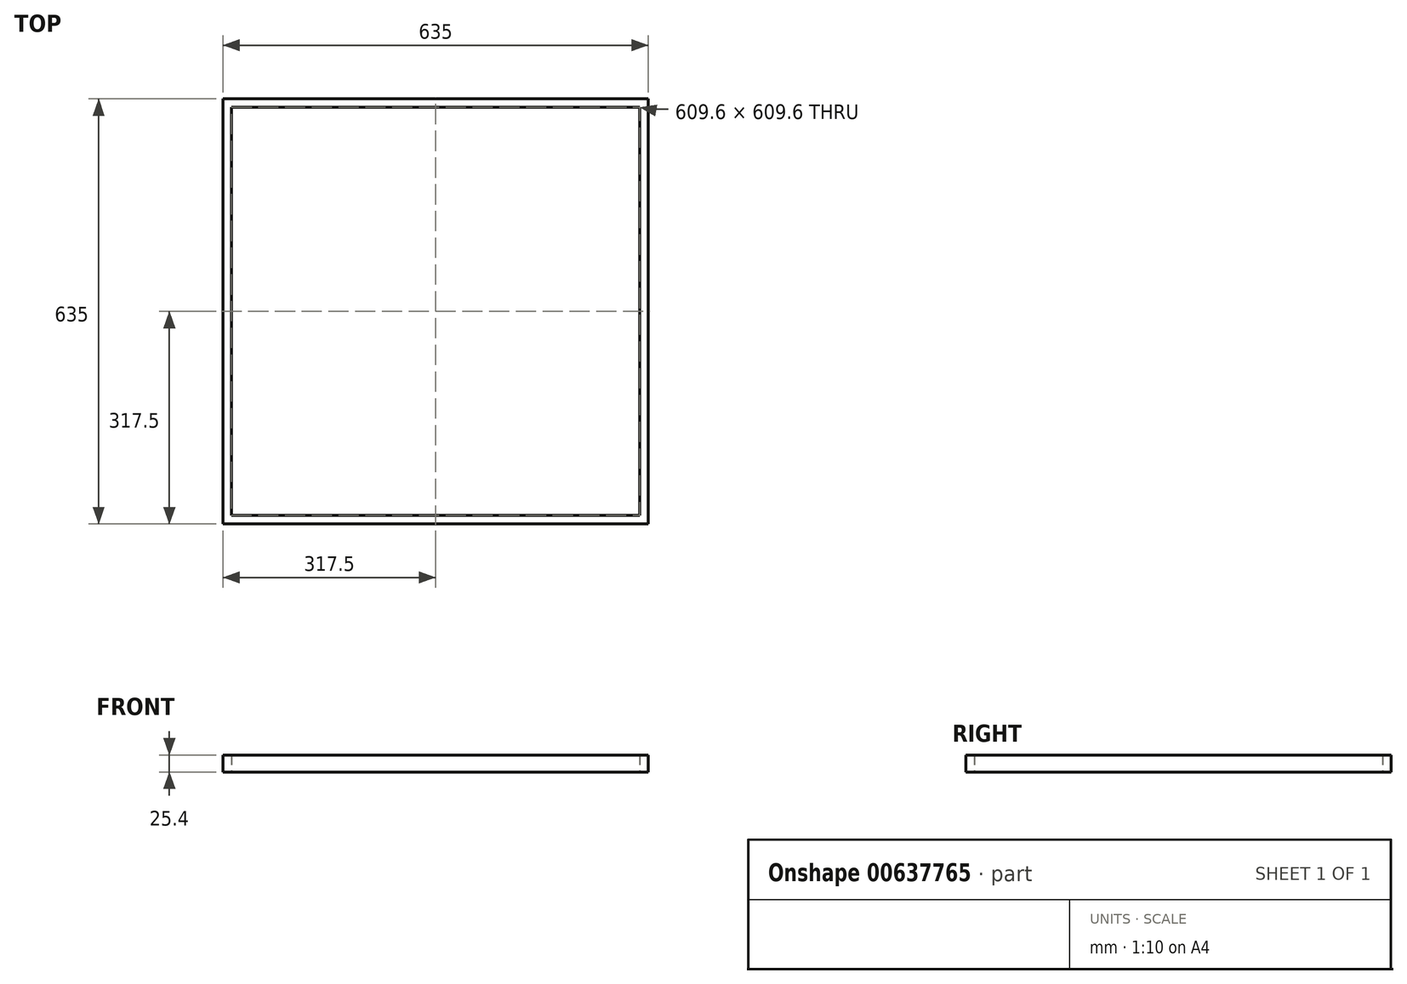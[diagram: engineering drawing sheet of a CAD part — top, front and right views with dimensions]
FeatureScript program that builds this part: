
annotation { "Feature Type Name" : "Feature", "Feature Type Description" : "" }
export const myFeature = defineFeature(function(context is Context, id is Id, definition is map)
    precondition{}
    {
        {
            var Q0;
            Q0=qCreatedBy(makeId("Top.planeOp"),FACE);
            var sketch = newSketch(context, id + "F0", { "sketchPlane" : qUnion([Q0])});
            skLineSegment(sketch, "E0.bottom", {"start": v(317.5, 317.5) * mm, "end": v(-317.5, 317.5) * mm});
            skLineSegment(sketch, "E0.top", {"start": v(317.5, -317.5) * mm, "end": v(-317.5, -317.5) * mm});
            skLineSegment(sketch, "E0.left", {"start": v(317.5, 317.5) * mm, "end": v(317.5, -317.5) * mm});
            skLineSegment(sketch, "E0.right", {"start": v(-317.5, 317.5) * mm, "end": v(-317.5, -317.5) * mm});
            skPoint(sketch, "E0.middle", {"position": v(0, 0) * mm});
            skSolve(sketch);
        }
        {
            var Q0;
            Q0=makeQuery(id+"F0.imprint","IMPRINT",FACE,{"disambiguationData":[TD([[makeQuery(id+"F0.imprint","IMPRINT",EDGE,{"derivedFrom":sQuery(id+"F0.wireOp",EDGE,"E0.bottom")}),1.0]])]});
            var sketch = newSketch(context, id + "F1", { "sketchPlane" : qUnion([Q0])});
            skLineSegment(sketch, "E1.bottom", {"start": v(304.8, -304.8) * mm, "end": v(-304.8, -304.8) * mm});
            skLineSegment(sketch, "E1.top", {"start": v(304.8, 304.8) * mm, "end": v(-304.8, 304.8) * mm});
            skLineSegment(sketch, "E1.left", {"start": v(304.8, -304.8) * mm, "end": v(304.8, 304.8) * mm});
            skLineSegment(sketch, "E1.right", {"start": v(-304.8, -304.8) * mm, "end": v(-304.8, 304.8) * mm});
            skPoint(sketch, "E1.middle", {"position": v(0, 0) * mm});
            skSolve(sketch);
        }
        {
            var Q0;
            Q0=makeQuery(id+"F1.imprint","IMPRINT",FACE,{"disambiguationData":[TD([[makeQuery(id+"F1.imprint","IMPRINT",EDGE,{"derivedFrom":sQuery(id+"F1.wireOp",EDGE,"E1.bottom")}),1.0]])]});
            extrude(context, id + "F2", {"entities" : qUnion([Q0]), "depth" : 25.4 * mm, "offsetDistance" : 25.4 * mm});
        }
    });
